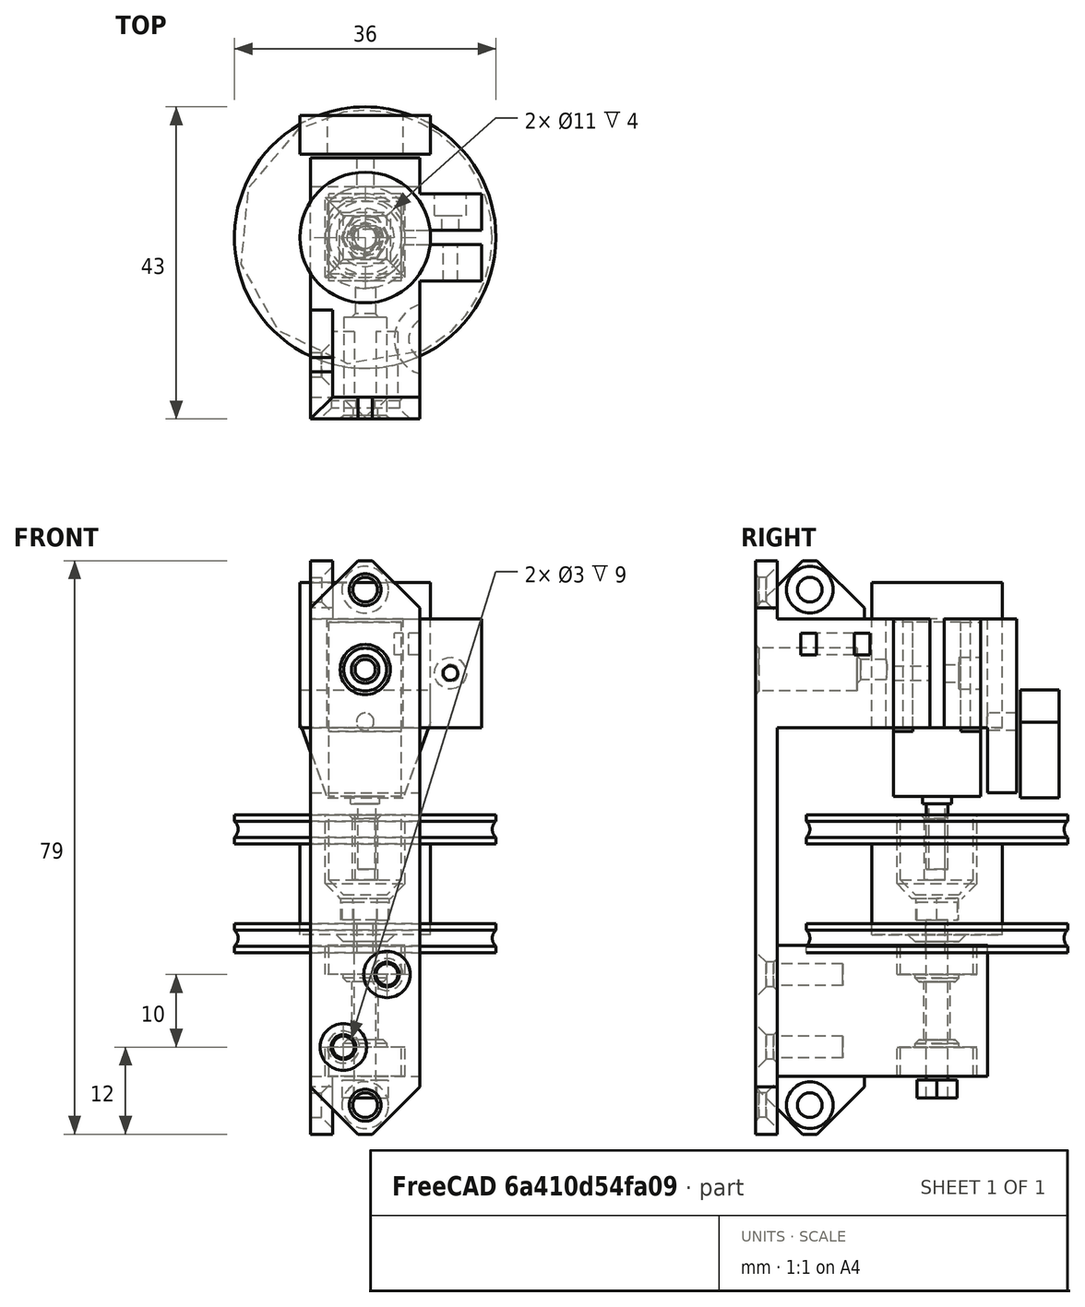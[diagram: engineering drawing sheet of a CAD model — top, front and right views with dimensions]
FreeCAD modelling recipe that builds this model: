
FCSTD DOCUMENT  (FreeCAD 0.18R16146 (Git))
Label: Motor and Opto Sensor Mount0.4
License: All rights reserved
LicenseURL: http://en.wikipedia.org/wiki/All_rights_reserved
objects: Part::Cylinder×35, Part::Cut×27, Part::Box×21, Part::Chamfer×16, Part::MultiFuse×15, Drawing::FeatureViewAnnotation×11, Part::Fuse×4, Part::Feature×3, Part::MultiCommon×2, Part::Torus×2, Part::Mirroring×2, Part::Cone×1, Drawing::FeaturePage×1
note: 128 computed .brp shape members not serialized (recipe doc carries the construction recipe); baked Part::Feature solids carry a one-line shape summary decoded from their .brp

FEATURE [Part::Box] Box406008004  label="gearbox004"
  AttacherType = Attacher::AttachEngine3D
  Height = 9
  Length = 12
  Placement = pos=(-6,-5,0) rot=(0,0,1;0rad)
  Width = 10
FEATURE [Part::Cylinder] Cylinder076  label="boss002"
  Angle = 360
  AttacherType = Attacher::AttachEngine3D
  Height = 1
  Placement = pos=(0,0,-1) rot=(0,0,1;0rad)
  Radius = 2
FEATURE [Part::Cylinder] Cylinder077
  Angle = 360
  AttacherType = Attacher::AttachEngine3D
  Height = 15
  Placement = pos=(0,0,9) rot=(0,0,1;0rad)
  Radius = 6
FEATURE [Part::Box] Box406008005  label="gearbox005"
  AttacherType = Attacher::AttachEngine3D
  Height = 27
  Length = 16
  Placement = pos=(-8,-5,0) rot=(0,0,1;0rad)
  Width = 10
FEATURE [Part::MultiCommon] Common001  label="motor002"
  Shapes = -> [Cylinder077,Box406008005]
FEATURE [Part::Cylinder] Cylinder078  label="shaft-002"
  Angle = 360
  AttacherType = Attacher::AttachEngine3D
  Height = 10
  Placement = pos=(0,0,-10) rot=(0,0,1;0rad)
  Radius = 1.5
FEATURE [Part::Box] Box406008006  label="Cube341"
  AttacherType = Attacher::AttachEngine3D
  Height = 12
  Length = 10
  Placement = pos=(-5,1,-11) rot=(0,0,1;0rad)
  Width = 10
FEATURE [Part::Cut] Cut001  label="shaft002"
  Base = -> Cylinder078
  Tool = -> Box406008006
FEATURE [Part::MultiFuse] Fusion103077013004017004  label="motor-assembled"
  Placement = pos=(0,0,20.5) rot=(0,0,1;1.5708rad)
  Shapes = -> [Box406008004,Cylinder076,Common001,Cut001]
FEATURE [Part::Cylinder] Cylinder028  label="Cylinder024"
  Angle = 360
  AttacherType = Attacher::AttachEngine3D
  Height = 10
  Placement = pos=(0,0,-1) rot=(0,0,1;0rad)
  Radius = 1.57
FEATURE [Part::Cylinder] Cylinder012  label="wheel1a"
  Angle = 360
  AttacherType = Attacher::AttachEngine3D
  Height = 4
  Radius = 18
FEATURE [Part::Box] Box084016  label="Cube067"
  AttacherType = Attacher::AttachEngine3D
  Height = 12
  Length = 10
  Placement = pos=(-5,1.1,-1.5) rot=(0,0,1;0rad)
  Width = 10
FEATURE [Part::Torus] Torus002
  Angle1 = -180
  Angle2 = 180
  Angle3 = 360
  AttacherType = Attacher::AttachEngine3D
  Placement = pos=(0,0,2) rot=(0,0,1;0rad)
  Radius1 = 19
  Radius2 = 1.5
FEATURE [Part::Cut] Cut057
  Base = -> Cylinder028
  Tool = -> Box084016
FEATURE [Part::Cut] Cut062
  Base = -> Cylinder012
  Tool = -> Cut057
FEATURE [Part::Cut] Cut063  label="wheel 0.1"
  Base = -> Cut062
  Placement = pos=(0,0,-1) rot=(0,0,1;0rad)
  Tool = -> Torus002
FEATURE [Part::Cylinder] Cylinder073  label="motor-bulge"
  Angle = 360
  AttacherType = Attacher::AttachEngine3D
  Height = 20
  Placement = pos=(0,0,30) rot=(0,0,1;0rad)
  Radius = 9
FEATURE [Part::Cylinder] Cylinder067
  Angle = 360
  AttacherType = Attacher::AttachEngine3D
  Height = 26
  Placement = pos=(0,0,20) rot=(0,0,1;0rad)
  Radius = 7
FEATURE [Part::Box] Box406017  label="gearbox001"
  AttacherType = Attacher::AttachEngine3D
  Height = 28
  Length = 16
  Placement = pos=(-8,-5.25,18) rot=(0,0,1;0rad)
  Width = 10.5
FEATURE [Part::MultiCommon] Common004  label="motor-hole"
  Placement = pos=(0,0,5) rot=(0,0,1;1.5708rad)
  Shapes = -> [Cylinder067,Box406017]
FEATURE [Part::Box] Box406016  label="clamp-slot"
  AttacherType = Attacher::AttachEngine3D
  Height = 32
  Length = 49
  Placement = pos=(48.48,1,22) rot=(0,0,1;3.14159rad)
  Width = 2
FEATURE [Part::Box] Box  label="Cube"
  AttacherType = Attacher::AttachEngine3D
  Height = 8
  Length = 15
  Placement = pos=(-7.5,-25,45) rot=(0,0,1;0rad)
  Width = 3
FEATURE [Part::Box] Box406008007  label="Cube342"
  AttacherType = Attacher::AttachEngine3D
  Height = 14.9
  Length = 18
  Placement = pos=(-9,13,34.3) rot=(0,0,1;0rad)
  Width = 5.3
FEATURE [Part::Cylinder] Cylinder079  label="Cylinder078"
  Angle = 360
  AttacherType = Attacher::AttachEngine3D
  Height = 17
  Placement = pos=(0,0,9) rot=(0,0,1;0rad)
  Radius = 1.75
FEATURE [Part::Box] Box406008008  label="Cube343"
  AttacherType = Attacher::AttachEngine3D
  Height = 19
  Length = 10
  Placement = pos=(-5,1.1,1.5) rot=(0,0,1;0rad)
  Width = 10
FEATURE [Part::Cut] Cut064  label="Motor Shaft Hole"
  Base = -> Cylinder079
  Tool = -> Box406008008
FEATURE [Part::Box] Box406008009  label="Cube344"
  AttacherType = Attacher::AttachEngine3D
  Height = 11
  Length = 10
  Placement = pos=(-5,-5,7) rot=(0,0,1;0rad)
  Width = 10
FEATURE [Part::Box] Box406008010  label="Cube345"
  AttacherType = Attacher::AttachEngine3D
  Height = 19.7
  Length = 17.5
  Placement = pos=(3.75,6,30.3) rot=(0,1,0;0.349066rad)
  Width = 13.3
FEATURE [Part::Box] Box406008011  label="Cube346"
  AttacherType = Attacher::AttachEngine3D
  Height = 19.7
  Length = 17.5
  Placement = pos=(3.75,6,30.3) rot=(0,1,0;0.349066rad)
  Width = 13.3
FEATURE [Part::Mirroring] Part__Mirroring  label="Cube346 (Mirror #1)"
  Base = (0,0,0)
  Normal = (1,0,0)
  Source = -> Box406008011
FEATURE [Part::MultiFuse] Fusion
  Shapes = -> [Box406008010,Part__Mirroring]
FEATURE [Part::Cut] Cut  label="Opto Sensor"
  Base = -> Box406008007
  Placement = pos=(0,-1.5,-14) rot=(0,0,1;0rad)
  Tool = -> Fusion
FEATURE [Part::Cut] Cut065  label="Square Peg"
  Base = -> Box406008009
  Tool = -> Cut064
FEATURE [Part::Box] Box406008012  label="Cube347"
  AttacherType = Attacher::AttachEngine3D
  Height = 11.5
  Length = 11
  Placement = pos=(-5.5,-5.5,6.5) rot=(0,0,1;0rad)
  Width = 11
FEATURE [Part::Cylinder] Cylinder
  Angle = 360
  AttacherType = Attacher::AttachEngine3D
  Height = 12.5
  Placement = pos=(0,0,1.5) rot=(0,0,1;0rad)
  Radius = 9
FEATURE [Part::Cylinder] Cylinder080  label="wheel1a001"
  Angle = 360
  AttacherType = Attacher::AttachEngine3D
  Height = 4
  Placement = pos=(0,0,14) rot=(0,0,1;0rad)
  Radius = 18
FEATURE [Part::Feature] Shape
  Placement = pos=(0,0,3.5) rot=(0,0,1;0rad)
  shape: bbox 6.697 x 5.8 x 15 mm, 8 faces (baked)
FEATURE [Part::MultiFuse] Fusion103077013004017005
  Shapes = -> [Cylinder080,Cylinder]
FEATURE [Part::Feature] Shape001
  Placement = pos=(0,0,3.5) rot=(0,0,1;0rad)
  shape: bbox 6.351 x 5.5 x 2.5 mm, 8 faces (baked)
FEATURE [Part::Cylinder] Cylinder081  label="Cylinder079"
  Angle = 360
  AttacherType = Attacher::AttachEngine3D
  Height = 25
  Placement = pos=(0,0,-21) rot=(0,0,1;0rad)
  Radius = 1.5
FEATURE [Part::MultiFuse] Fusion103077013004017006  label="M3 x 25 Hex Head"
  Shapes = -> [Shape001,Cylinder081]
FEATURE [Part::Cut] Cut066
  Base = -> Fusion103077013004017005
  Tool = -> Box406008012
FEATURE [Part::Cone] Cone
  Angle = 360
  AttacherType = Attacher::AttachEngine3D
  Height = 1
  Placement = pos=(0,0,0.5) rot=(0,0,1;0rad)
  Radius1 = 3
  Radius2 = 4
FEATURE [Part::MultiFuse] Fusion103077013004017007
  Shapes = -> [Cut066,Cone]
FEATURE [Part::Cut] Cut067
  Base = -> Fusion103077013004017007
  Tool = -> Shape
FEATURE [Part::Cylinder] Cylinder082  label="623 Bearing"
  Angle = 360
  AttacherType = Attacher::AttachEngine3D
  Height = 4
  Placement = pos=(0,0,-4) rot=(0,0,1;0rad)
  Radius = 5
FEATURE [Part::Cylinder] Cylinder083  label="623 Bearing001"
  Angle = 360
  AttacherType = Attacher::AttachEngine3D
  Height = 4
  Placement = pos=(0,0,-18) rot=(0,0,1;0rad)
  Radius = 5
FEATURE [Part::Feature] Shape002  label="Nylock"
  Placement = pos=(0,0,-21) rot=(0,0,1;0rad)
  shape: bbox 6.351 x 5.5 x 2.5 mm, 8 faces (baked)
FEATURE [Part::Cylinder] Cylinder084  label="Cylinder080"
  Angle = 360
  AttacherType = Attacher::AttachEngine3D
  Height = 6
  Placement = pos=(0,0,-2) rot=(0,0,1;0rad)
  Radius = 1.5
FEATURE [Part::Cut] Cut069
  Base = -> Cut067
  Tool = -> Cylinder084
FEATURE [Part::Cylinder] Cylinder085  label="Cylinder081"
  Angle = 360
  AttacherType = Attacher::AttachEngine3D
  Height = 12
  Placement = pos=(0,0,-14) rot=(0,0,1;0rad)
  Radius = 1.8
FEATURE [Part::Box] Box406008013  label="Cube348"
  AttacherType = Attacher::AttachEngine3D
  Height = 18
  Length = 15
  Placement = pos=(-7.5,-22,-18) rot=(0,0,1;0rad)
  Width = 29
FEATURE [Part::Cylinder] Cylinder086  label="623 Bearing002"
  Angle = 360
  AttacherType = Attacher::AttachEngine3D
  Height = 4
  Placement = pos=(0,0,-4) rot=(0,0,1;0rad)
  Radius = 5.5
FEATURE [Part::Cylinder] Cylinder087  label="623 Bearing003"
  Angle = 360
  AttacherType = Attacher::AttachEngine3D
  Height = 4
  Placement = pos=(0,0,-18) rot=(0,0,1;0rad)
  Radius = 5.5
FEATURE [Part::MultiFuse] Fusion103077013004017008  label="623 Bearing Holes"
  Shapes = -> [Cylinder086,Cylinder087]
FEATURE [Part::Cut] Cut070
  Base = -> Box406008013
  Tool = -> Fusion103077013004017008
FEATURE [Part::Cylinder] Cylinder088  label="Cylinder082"
  Angle = 360
  AttacherType = Attacher::AttachEngine3D
  Height = 1
  Placement = pos=(0,0,-5) rot=(0,0,1;0rad)
  Radius = 3
FEATURE [Part::Cylinder] Cylinder089  label="Cylinder083"
  Angle = 360
  AttacherType = Attacher::AttachEngine3D
  Height = 1
  Placement = pos=(0,0,-14) rot=(0,0,1;0rad)
  Radius = 3
FEATURE [Part::MultiFuse] Fusion103077013004017009
  Shapes = -> [Cylinder089,Cylinder088]
FEATURE [Part::Cut] Cut071
  Base = -> Cut070
  Tool = -> Fusion103077013004017009
FEATURE [Part::Cut] Cut072
  Base = -> Cut071
  Tool = -> Cylinder085
FEATURE [Part::Chamfer] Chamfer
  Base = -> Cut072
  Edges = 1 edges r=0.5: [Edge22]
FEATURE [Part::Chamfer] Chamfer001  label="Bearing Mount end"
  Base = -> Chamfer
  Edges = 1 edges r=0.5: [Edge16]
FEATURE [Part::Box] Box406008014  label="Cube349"
  AttacherType = Attacher::AttachEngine3D
  Height = 63
  Length = 15
  Placement = pos=(-7.5,-25,-18) rot=(0,0,1;0rad)
  Width = 3
FEATURE [Part::Box] Box406008015  label="Cube350"
  AttacherType = Attacher::AttachEngine3D
  Height = 15
  Length = 15
  Placement = pos=(-7.5,-22,35) rot=(0,0,1;0rad)
  Width = 31
FEATURE [Part::Cut] Cut073
  Base = -> Box406008015
  Tool = -> Common004
FEATURE [Part::Cylinder] Cylinder068
  Angle = 360
  AttacherType = Attacher::AttachEngine3D
  Height = 12
  Placement = pos=(11.75,0,42.5) rot=(0,0.707106,0.707107;3.14159rad)
  Radius = 1.2
FEATURE [Part::Cylinder] Cylinder069
  Angle = 360
  AttacherType = Attacher::AttachEngine3D
  Height = 12
  Placement = pos=(11.75,3,42.5) rot=(0,0.707106,0.707107;3.14159rad)
  Radius = 2.2
FEATURE [Part::MultiFuse] Fusion103077013  label="M2-screw001"
  Shapes = -> [Cylinder068,Cylinder069]
FEATURE [Part::Box] Box406008016  label="Cube351"
  AttacherType = Attacher::AttachEngine3D
  Height = 15
  Length = 9
  Placement = pos=(7,-6,35) rot=(0,0,1;0rad)
  Width = 12
FEATURE [Part::Fuse] Fusion103077013004017010
  Base = -> Cut073
  Tool = -> Box406008016
FEATURE [Part::Cut] Cut074
  Base = -> Fusion103077013004017010
  Tool = -> Box406016
FEATURE [Part::Box] Box406008017  label="Cube352"
  AttacherType = Attacher::AttachEngine3D
  Height = 24
  Length = 15
  Placement = pos=(-7.5,7,26) rot=(0,0,1;0rad)
  Width = 4
FEATURE [Part::Cylinder] Cylinder090  label="Cylinder084"
  Angle = 360
  AttacherType = Attacher::AttachEngine3D
  Height = 13
  Placement = pos=(0,16,35.8) rot=(1,0,0;1.5708rad)
  Radius = 1.2
FEATURE [Part::Cylinder] Cylinder091
  Angle = 360
  AttacherType = Attacher::AttachEngine3D
  Height = 12
  Placement = pos=(11.75,-12,42.5) rot=(0,0.707106,0.707107;3.14159rad)
  Radius = 1
FEATURE [Part::Fuse] Fusion103077013004017011
  Base = -> Fusion103077013
  Tool = -> Cylinder091
FEATURE [Part::Cut] Cut075
  Base = -> Cut074
  Tool = -> Fusion103077013004017011
FEATURE [Part::Fuse] Fusion103077013004017012
  Base = -> Box406008017
  Tool = -> Cut075
FEATURE [Part::Cut] Cut076  label="Motor Mount 0.2"
  Base = -> Fusion103077013004017012
  Placement = pos=(0,0,-5) rot=(0,0,1;0rad)
  Tool = -> Cylinder090
FEATURE [Part::Cylinder] Cylinder092
  Angle = 360
  AttacherType = Attacher::AttachEngine3D
  Height = 21
  Placement = pos=(-3,-13,-14) rot=(1,0,0;1.5708rad)
  Radius = 1.7
FEATURE [Part::Cylinder] Cylinder093
  Angle = 360
  AttacherType = Attacher::AttachEngine3D
  Height = 21
  Placement = pos=(3,-13,-4) rot=(1,0,0;1.5708rad)
  Radius = 1.7
FEATURE [Part::Cylinder] Cylinder094
  Angle = 360
  AttacherType = Attacher::AttachEngine3D
  Height = 21
  Placement = pos=(-3,-13,-14) rot=(1,0,0;1.5708rad)
  Radius = 1.5
FEATURE [Part::Cylinder] Cylinder095
  Angle = 360
  AttacherType = Attacher::AttachEngine3D
  Height = 21
  Placement = pos=(3,-13,-4) rot=(1,0,0;1.5708rad)
  Radius = 1.5
FEATURE [Part::MultiFuse] Fusion103077013004017013
  Shapes = -> [Cylinder092,Cylinder093]
FEATURE [Part::Cut] Cut077
  Base = -> Box406008014
  Tool = -> Fusion103077013004017013
FEATURE [Part::MultiFuse] Fusion103077013004017014
  Shapes = -> [Cylinder094,Cylinder095]
FEATURE [Part::Cut] Cut078  label="Bearing Mount End 0.2"
  Base = -> Chamfer001
  Tool = -> Fusion103077013004017014
FEATURE [Part::Cylinder] Cylinder096
  Angle = 360
  AttacherType = Attacher::AttachEngine3D
  Height = 21
  Placement = pos=(0,-13,49) rot=(1,0,0;1.5708rad)
  Radius = 1.7
FEATURE [Part::Cylinder] Cylinder097
  Angle = 360
  AttacherType = Attacher::AttachEngine3D
  Height = 21
  Placement = pos=(0,-13,-22) rot=(1,0,0;1.5708rad)
  Radius = 1.7
FEATURE [Part::Chamfer] Chamfer003  label="Wheel"
  Base = -> Cut069
  Edges = 4 edges r=2: [Edge11,Edge12,Edge15,Edge16]
FEATURE [Part::Chamfer] Chamfer004  label="Square Peg001"
  Base = -> Cut065
  Edges = 4 edges r=2: [Edge4,Edge5,Edge13,Edge15]
FEATURE [Part::Box] Box406008018  label="Cube353"
  AttacherType = Attacher::AttachEngine3D
  Height = 8
  Length = 15
  Placement = pos=(-7.5,-25,-26) rot=(0,0,1;0rad)
  Width = 3
FEATURE [Part::Cut] Cut079
  Base = -> Box406008018
  Tool = -> Cylinder097
FEATURE [Part::Cut] Cut080
  Base = -> Box
  Tool = -> Cylinder096
FEATURE [Part::MultiFuse] Fusion103077013004017015
  Shapes = -> [Cut079,Cut080]
FEATURE [Part::Chamfer] Chamfer005  label="Chamfer005 mount holes"
  Base = -> Fusion103077013004017015
  Edges = 2 edges r=1.5: [Edge13,Edge28]
FEATURE [Part::Chamfer] Chamfer006  label="Chamfer under side CS screw holes"
  Base = -> Cut077
  Edges = 2 edges r=1.5: [Edge8,Edge9]
FEATURE [Part::MultiFuse] Fusion103077013004017016
  Shapes = -> [Chamfer006,Chamfer005]
FEATURE [Part::Chamfer] Chamfer007  label="Chamfer Corner edges of mount"
  Base = -> Fusion103077013004017016
  Edges = 4 edges r=6.5: [Edge27,Edge29,Edge34,Edge39]
FEATURE [Part::Cylinder] Cylinder098
  Angle = 360
  AttacherType = Attacher::AttachEngine3D
  Height = 3
  Placement = pos=(-9,-9,36) rot=(1,0,0;0rad)
  Radius = 5
FEATURE [Part::Cylinder] Cylinder099
  Angle = 360
  AttacherType = Attacher::AttachEngine3D
  Height = 3
  Placement = pos=(-9,-9,36) rot=(1,0,0;0rad)
  Radius = 3
FEATURE [Part::Cut] Cut081  label="Cable tie Hole"
  Base = -> Cylinder098
  Placement = pos=(18,-5,4) rot=(0,0,1;0rad)
  Tool = -> Cylinder099
FEATURE [Part::Cut] Cut082
  Base = -> Cut076
  Tool = -> Cut081
FEATURE [Part::MultiFuse] Fusion103077013004017017
  Shapes = -> [Chamfer007,Cut082]
FEATURE [Drawing::FeatureViewAnnotation] Annotation
  Font = Sans
  Rotation = 0
  Scale = 7
  Text = Square Peg 0.1 - 0.2 Hole R 1.57 -> 1.75 and chamfered
  ViewResult = <g transform="translate(10,20) rotate(0)">\n<text id="Annotation"\n font-family="Sans"\n font-size="7"\n fill="#000000">\n<tspan x="0" dy="1em">Square Peg 0.1 - 0.2 Hole R 1.57 -> 1.75 and chamfered</tspan>\n</text>\n</g>
  Visible = true
  X = 10
  Y = 20
FEATURE [Part::Chamfer] Chamfer008  label="Square Peg 0.2"
  Base = -> Chamfer004
  Edges = 3 edges r=0.5: [Edge13,Edge14,Edge15]
FEATURE [Drawing::FeatureViewAnnotation] Annotation001
  Font = Sans
  Rotation = 0
  Scale = 7
  Text = Bearing Mount End 0.2 0 Hole R 1.5 -> 1.8
  ViewResult = <g transform="translate(10,60) rotate(0)">\n<text id="Annotation001"\n font-family="Sans"\n font-size="7"\n fill="#000000">\n<tspan x="0" dy="1em">Bearing Mount End 0.2 0 Hole R 1.5 -> 1.8</tspan>\n</text>\n</g>
  Visible = true
  X = 10
  Y = 60
FEATURE [Drawing::FeatureViewAnnotation] Annotation002
  Font = Sans
  Rotation = 0
  Scale = 7
  Text = Motor Mount Hole 6.25 -> 7mm
  ViewResult = <g transform="translate(10,40) rotate(0)">\n<text id="Annotation002"\n font-family="Sans"\n font-size="7"\n fill="#000000">\n<tspan x="0" dy="1em">Motor Mount Hole 6.25 -> 7mm</tspan>\n</text>\n</g>
  Visible = true
  X = 10
  Y = 40
FEATURE [Part::Chamfer] Chamfer009  label="Chamfer on bottom of mount holes (so they print better)"
  Base = -> Fusion103077013004017017
  Edges = 2 edges r=0.5: [Edge46,Edge47]
FEATURE [Part::Chamfer] Chamfer010  label="Motor and Opto Sensor Mount 0.2"
  Base = -> Chamfer009
  Edges = 2 edges r=0.5: [Edge102,Edge107]
FEATURE [Drawing::FeatureViewAnnotation] Annotation003
  Font = Sans
  Rotation = 0
  Scale = 7
  Text = Chamfered holes that are printed sideways
  ViewResult = <g transform="translate(10,80) rotate(0)">\n<text id="Annotation003"\n font-family="Sans"\n font-size="7"\n fill="#000000">\n<tspan x="0" dy="1em">Chamfered holes that are printed sideways</tspan>\n</text>\n</g>
  Visible = true
  X = 10
  Y = 80
FEATURE [Part::Cylinder] Cylinder100
  Angle = 360
  AttacherType = Attacher::AttachEngine3D
  Height = 28
  Placement = pos=(0,0,38) rot=(1,0,0;1.5708rad)
  Radius = 1.4
FEATURE [Drawing::FeatureViewAnnotation] Annotation004
  Font = Sans
  Rotation = 0
  Scale = 7
  Text = 0.2 -> 0.3 Changes
  ViewResult = <g transform="translate(10,100) rotate(0)">\n<text id="Annotation004"\n font-family="Sans"\n font-size="7"\n fill="#000000">\n<tspan x="0" dy="1em">0.2 -> 0.3 Changes</tspan>\n</text>\n</g>
  Visible = true
  X = 10
  Y = 100
FEATURE [Drawing::FeatureViewAnnotation] Annotation005
  Font = Sans
  Rotation = 0
  Scale = 7
  Text = Hole to hold motor
  ViewResult = <g transform="translate(20,120) rotate(0)">\n<text id="Annotation005"\n font-family="Sans"\n font-size="7"\n fill="#000000">\n<tspan x="0" dy="1em">Hole to hold motor</tspan>\n</text>\n</g>
  Visible = true
  X = 20
  Y = 120
FEATURE [Part::Cylinder] Cylinder101
  Angle = 360
  AttacherType = Attacher::AttachEngine3D
  Height = 20
  Placement = pos=(0,-11,38) rot=(1,0,0;1.5708rad)
  Radius = 2.95
FEATURE [Part::MultiFuse] Fusion103077013004017018
  Shapes = -> [Cylinder100,Cylinder101]
FEATURE [Part::Cylinder] Cylinder102
  Angle = 360
  AttacherType = Attacher::AttachEngine3D
  Height = 21
  Placement = pos=(-15,-17.5,-22) rot=(0,1,0;1.5708rad)
  Radius = 1.7
FEATURE [Part::Box] Box406008019  label="Cube354"
  AttacherType = Attacher::AttachEngine3D
  Height = 8
  Length = 15
  Placement = pos=(-4.5,-25,-26) rot=(0,0,1;1.5708rad)
  Width = 3
FEATURE [Part::Cut] Cut083
  Base = -> Box406008019
  Tool = -> Cylinder102
FEATURE [Part::Chamfer] Chamfer011  label="Chamfer Mount corner edges"
  Base = -> Cut083
  Edges = 2 edges r=6.5: [Edge4,Edge14]
FEATURE [Part::Chamfer] Chamfer012  label="Chamfer012 Mount Hole"
  Base = -> Chamfer011
  Edges = 1 edges r=1.5: [Edge10]
FEATURE [Part::Cylinder] Cylinder103
  Angle = 360
  AttacherType = Attacher::AttachEngine3D
  Height = 21
  Placement = pos=(-15,-17.5,-22) rot=(0,1,0;1.5708rad)
  Radius = 1.7
FEATURE [Part::Box] Box406008020  label="Cube355"
  AttacherType = Attacher::AttachEngine3D
  Height = 8
  Length = 15
  Placement = pos=(-4.5,-25,-26) rot=(0,0,1;1.5708rad)
  Width = 3
FEATURE [Part::Cut] Cut084
  Base = -> Box406008020
  Tool = -> Cylinder103
FEATURE [Part::Chamfer] Chamfer013  label="Chamfer Mount corner edges001"
  Base = -> Cut084
  Edges = 2 edges r=6.5: [Edge4,Edge14]
FEATURE [Part::Chamfer] Chamfer014  label="Chamfer012 Mount Hole001"
  Base = -> Chamfer013
  Edges = 1 edges r=1.5: [Edge10]
FEATURE [Part::Mirroring] Part__Mirroring001  label="Chamfer012 Mount Hole001 (Mirror #2)"
  Base = (0,0,0)
  Normal = (0,0,1)
  Placement = pos=(0,0,27) rot=(0,0,1;0rad)
  Source = -> Chamfer014
FEATURE [Drawing::FeatureViewAnnotation] Annotation006
  Font = Sans
  Rotation = 0
  Scale = 7
  Text = Additional mounts at 90 degrees
  ViewResult = <g transform="translate(20,140) rotate(0)">\n<text id="Annotation006"\n font-family="Sans"\n font-size="7"\n fill="#000000">\n<tspan x="0" dy="1em">Additional mounts at 90 degrees</tspan>\n</text>\n</g>
  Visible = true
  X = 20
  Y = 140
FEATURE [Drawing::FeatureViewAnnotation] Annotation007
  Font = Sans
  Rotation = 0
  Scale = 7
  Text = Switched Cable tie hole and offset
  ViewResult = <g transform="translate(20,160) rotate(0)">\n<text id="Annotation007"\n font-family="Sans"\n font-size="7"\n fill="#000000">\n<tspan x="0" dy="1em">Switched Cable tie hole and offset</tspan>\n</text>\n</g>
  Visible = true
  X = 20
  Y = 160
FEATURE [Part::Cut] Cut085
  Base = -> Chamfer010
  Tool = -> Fusion103077013004017018
FEATURE [Part::MultiFuse] Fusion103077013004017019
  Shapes = -> [Part__Mirroring001,Chamfer012]
FEATURE [Part::Fuse] Fusion103077013004017020
  Base = -> Cut085
  Tool = -> Fusion103077013004017019
FEATURE [Part::Chamfer] Chamfer015
  Base = -> Fusion103077013004017020
  Edges = 1 edges r=0.5: [Edge97]
FEATURE [Part::Chamfer] Chamfer016  label="Motor and Opto Sensor Mount 0.4"
  Base = -> Chamfer015
  Edges = 1 edges r=0.5: [Edge5]
FEATURE [Part::Torus] Torus003
  Angle1 = -180
  Angle2 = 180
  Angle3 = 360
  AttacherType = Attacher::AttachEngine3D
  Placement = pos=(0,0,16) rot=(0,0,1;0rad)
  Radius1 = 19
  Radius2 = 1.5
FEATURE [Part::Cut] Cut086  label="Wheel 0.4"
  Base = -> Chamfer003
  Tool = -> Torus003
FEATURE [Drawing::FeatureViewAnnotation] Annotation008
  Font = Sans
  Rotation = 0
  Scale = 7
  Text = 0.3->0.4
  ViewResult = <g transform="translate(10,180) rotate(0)">\n<text id="Annotation008"\n font-family="Sans"\n font-size="7"\n fill="#000000">\n<tspan x="0" dy="1em">0.3->0.4</tspan>\n</text>\n</g>
  Visible = true
  X = 10
  Y = 180
FEATURE [Drawing::FeatureViewAnnotation] Annotation009
  Font = Sans
  Rotation = 0
  Scale = 7
  Text = Added (subtracted) Torus from the wheel
  ViewResult = <g transform="translate(10,200) rotate(0)">\n<text id="Annotation009"\n font-family="Sans"\n font-size="7"\n fill="#000000">\n<tspan x="0" dy="1em">Added (subtracted) Torus from the wheel</tspan>\n</text>\n</g>
  Visible = true
  X = 10
  Y = 200
FEATURE [Drawing::FeatureViewAnnotation] Annotation010
  Font = Sans
  Rotation = 0
  Scale = 7
  Text = Changed S. Tapping hole on Motor Mount End from 1.7 to 1.4  
  ViewResult = <g transform="translate(10,220) rotate(0)">\n<text id="Annotation010"\n font-family="Sans"\n font-size="7"\n fill="#000000">\n<tspan x="0" dy="1em">Changed S. Tapping hole on Motor Mount End from 1.7 to 1.4  </tspan>\n</text>\n</g>
  Visible = true
  X = 10
  Y = 220
FEATURE [Drawing::FeaturePage] Page
  EditableTexts = AUTHOR NAME | CREATION DATE | SUPERVISOR NAME | CHECK DATE | SCALE | WEIGHT | NUMBER | SHEET | TITLE | SUBTITLE
  Group = -> [Annotation,Annotation001,Annotation002,Annotation003,Annotation004,Annotation005,Annotation006,Annotation007,Annotation008,Annotation009,Annotation010]
  Template = <path>
note: 1 file-system path scrubbed to <path> (originals preserved in the JSON sidecar)
